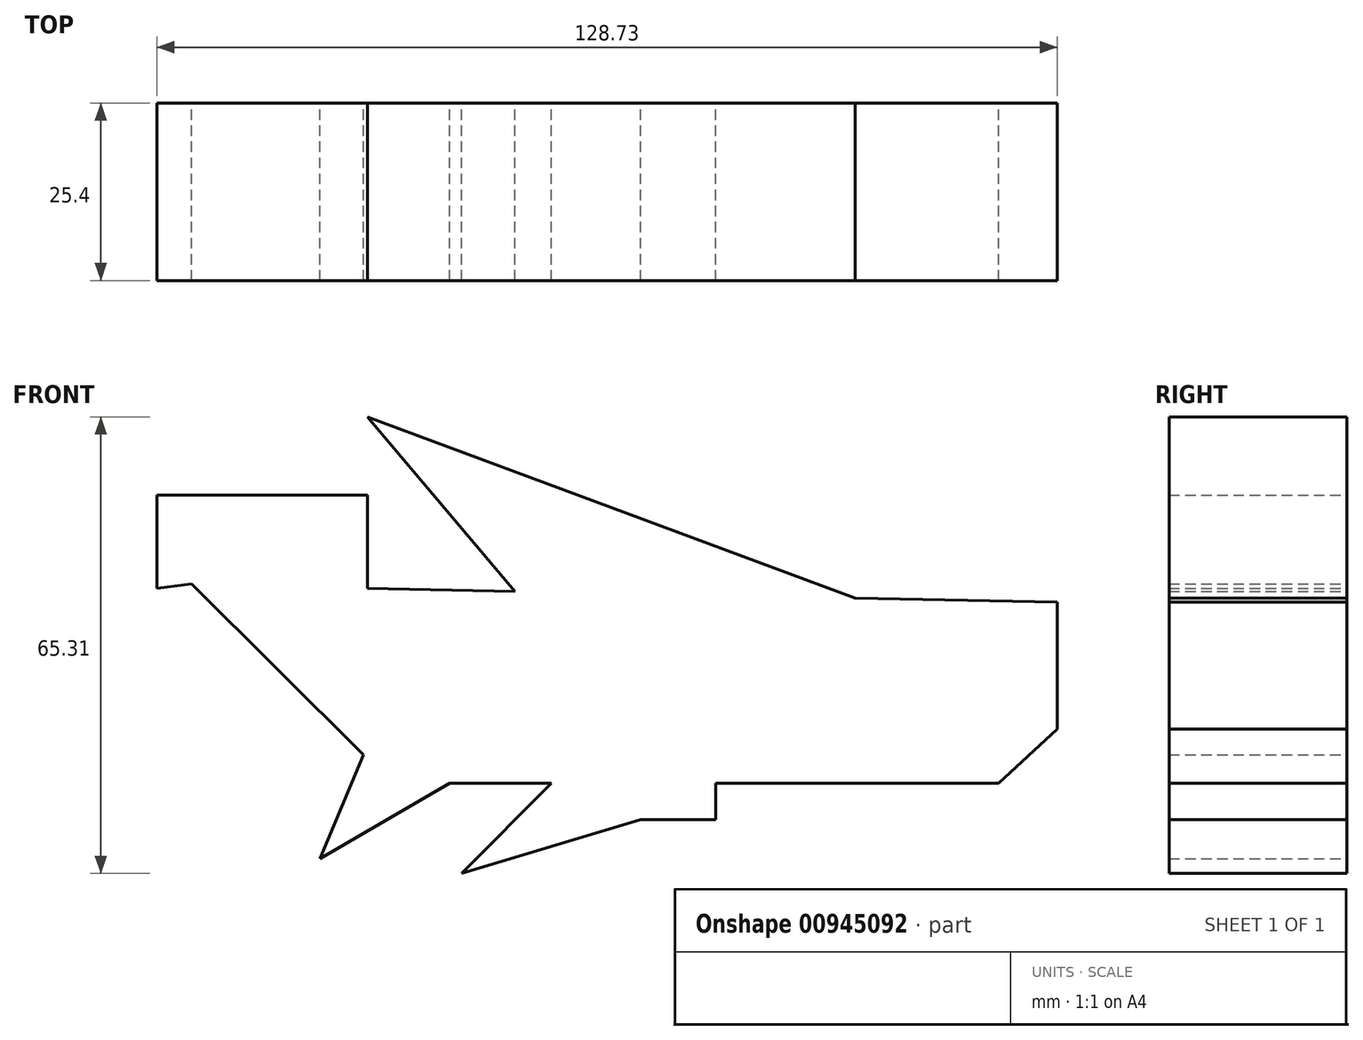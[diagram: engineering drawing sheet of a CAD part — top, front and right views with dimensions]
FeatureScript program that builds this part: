
annotation { "Feature Type Name" : "Feature", "Feature Type Description" : "" }
export const myFeature = defineFeature(function(context is Context, id is Id, definition is map)
    precondition{}
    {
        {
            var Q0;
            Q0=qCreatedBy(makeId("Front.planeOp"),FACE);
            var sketch = newSketch(context, id + "F0", { "sketchPlane" : qUnion([Q0])});
            skLineSegment(sketch, "E0", {"start": v(-55.5, 8.77) * mm, "end": v(-26.8, -19.73) * mm});
            skLineSegment(sketch, "E1", {"start": v(-26.8, -19.73) * mm, "end": v(59.88, -19.73) * mm});
            skLineSegment(sketch, "E2", {"start": v(59.88, -19.73) * mm, "end": v(68.25, -11.96) * mm});
            skLineSegment(sketch, "E3", {"start": v(68.25, -11.96) * mm, "end": v(68.25, 6.18) * mm});
            skLineSegment(sketch, "E4", {"start": v(68.25, 6.18) * mm, "end": v(-30.39, 8.17) * mm});
            skLineSegment(sketch, "E5", {"start": v(-30.39, 8.17) * mm, "end": v(-30.39, 21.52) * mm});
            skLineSegment(sketch, "E6", {"start": v(-30.39, 21.52) * mm, "end": v(-60.48, 21.52) * mm});
            skLineSegment(sketch, "E7", {"start": v(-60.48, 21.52) * mm, "end": v(-60.48, 8.17) * mm});
            skLineSegment(sketch, "E8", {"start": v(-60.48, 8.17) * mm, "end": v(-55.5, 8.77) * mm});
            skLineSegment(sketch, "E9", {"start": v(-9.28, 7.74) * mm, "end": v(-30.39, 32.68) * mm});
            skLineSegment(sketch, "E10", {"start": v(-30.39, 32.68) * mm, "end": v(39.35, 6.76) * mm});
            skLineSegment(sketch, "E11", {"start": v(-30.9, -15.66) * mm, "end": v(-37.17, -30.49) * mm});
            skLineSegment(sketch, "E12", {"start": v(-37.17, -30.49) * mm, "end": v(-18.63, -19.73) * mm});
            skLineSegment(sketch, "E13", {"start": v(-4.09, -19.73) * mm, "end": v(-16.9, -32.63) * mm});
            skLineSegment(sketch, "E14", {"start": v(-16.9, -32.63) * mm, "end": v(8.67, -24.9) * mm});
            skLineSegment(sketch, "E15", {"start": v(8.67, -24.9) * mm, "end": v(19.43, -24.9) * mm});
            skLineSegment(sketch, "E16", {"start": v(19.43, -24.9) * mm, "end": v(19.43, -19.73) * mm});
            skSolve(sketch);
        }
        {
            var Q0;
            Q0=makeQuery(id+"F0.imprint","IMPRINT",FACE,{"disambiguationData":[TD([[makeQuery(id+"F0.imprint","IMPRINT",EDGE,{"derivedFrom":sQuery(id+"F0.wireOp",EDGE,"E0")}),1.0]])]});
            var Q1;
            {var subQ0=sQuery(id+"F0.wireOp",EDGE,"E9");Q1=makeQuery(id+"F0.imprint","IMPRINT",FACE,{"disambiguationData":[TD([[makeQuery(id+"F0.imprint","IMPRINT",EDGE,{"derivedFrom":subQ0}),-1.0]])]});}
            var Q2;
            {var subQ0=sQuery(id+"F0.wireOp",EDGE,"E13");Q2=makeQuery(id+"F0.imprint","IMPRINT",FACE,{"disambiguationData":[TD([[makeQuery(id+"F0.imprint","IMPRINT",EDGE,{"derivedFrom":subQ0}),1.0]])]});}
            var Q3;
            {var subQ3=sQuery(id+"F0.wireOp",EDGE,"E11");Q3=makeQuery(id+"F0.imprint","IMPRINT",FACE,{"disambiguationData":[TD([[makeQuery(id+"F0.imprint","IMPRINT",EDGE,{"derivedFrom":subQ3}),1.0]])]});}
            extrude(context, id + "F1", {"entities" : qUnion([Q0, Q1, Q2, Q3]), "depth" : 25.4 * mm, "offsetDistance" : 25.4 * mm});
        }
    });
